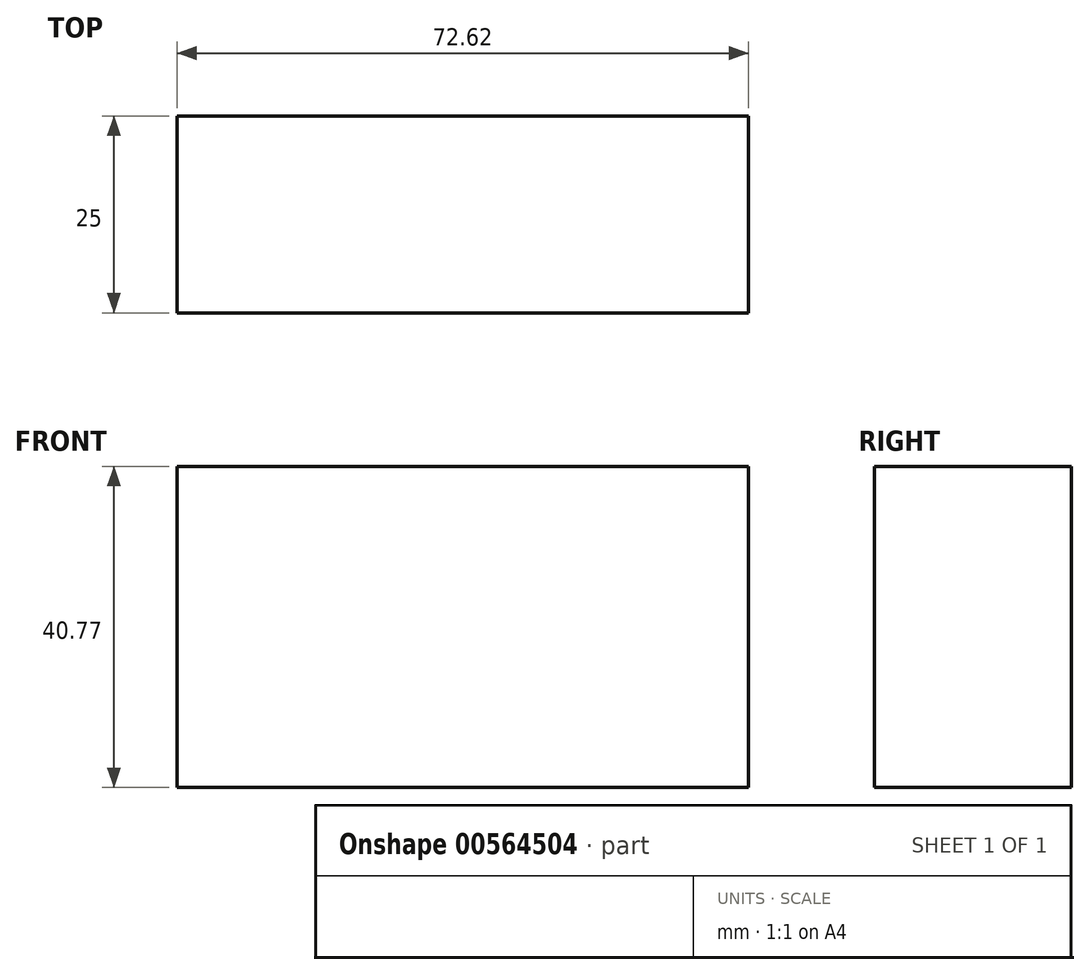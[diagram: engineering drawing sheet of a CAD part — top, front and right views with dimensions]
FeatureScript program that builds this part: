
annotation { "Feature Type Name" : "Feature", "Feature Type Description" : "" }
export const myFeature = defineFeature(function(context is Context, id is Id, definition is map)
    precondition{}
    {
        {
            var Q0;
            Q0=qCreatedBy(makeId("Front.planeOp"),FACE);
            var sketch = newSketch(context, id + "F0", { "sketchPlane" : qUnion([Q0])});
            skLineSegment(sketch, "E0.bottom", {"start": v(-19.8, 35.78) * mm, "end": v(52.81, 35.78) * mm});
            skLineSegment(sketch, "E0.top", {"start": v(-19.8, 76.55) * mm, "end": v(52.81, 76.55) * mm});
            skLineSegment(sketch, "E0.left", {"start": v(-19.8, 35.78) * mm, "end": v(-19.8, 76.55) * mm});
            skLineSegment(sketch, "E0.right", {"start": v(52.81, 35.78) * mm, "end": v(52.81, 76.55) * mm});
            skSolve(sketch);
        }
        {
            var Q0;
            Q0=makeQuery(id+"F0.imprint","IMPRINT",FACE,{"disambiguationData":[TD([[makeQuery(id+"F0.imprint","IMPRINT",EDGE,{"derivedFrom":sQuery(id+"F0.wireOp",EDGE,"E0.bottom")}),1.0]])]});
            extrude(context, id + "F1", {"entities" : qUnion([Q0]), "depth" : 25 * mm, "offsetDistance" : 25 * mm});
        }
    });
